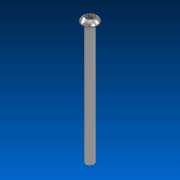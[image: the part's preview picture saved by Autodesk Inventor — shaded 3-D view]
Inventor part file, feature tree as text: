
AUTODESK INVENTOR PART (.ipt)
format: ipt  version: 2022.2 (Build 262287000, 287)  size: 155,136 bytes
history: native  units: in
note: dims shown in document units (in); Inventor stores cm internally (conversion verified against a paired STEP export)
features: direct_edit x1, chamfer x1, move_body x1
ambient origin geometry x8: Origin, YZ Plane, XZ Plane, XY Plane, X Axis, Y Axis, Z Axis, Center Point
bodies: Solid1 (feature_tree)
feature tree (3):
  direct_edit  "Direct Edit1"
  chamfer  "Chamfer2"  Distance=0.25in
  move_body  "Move1"
